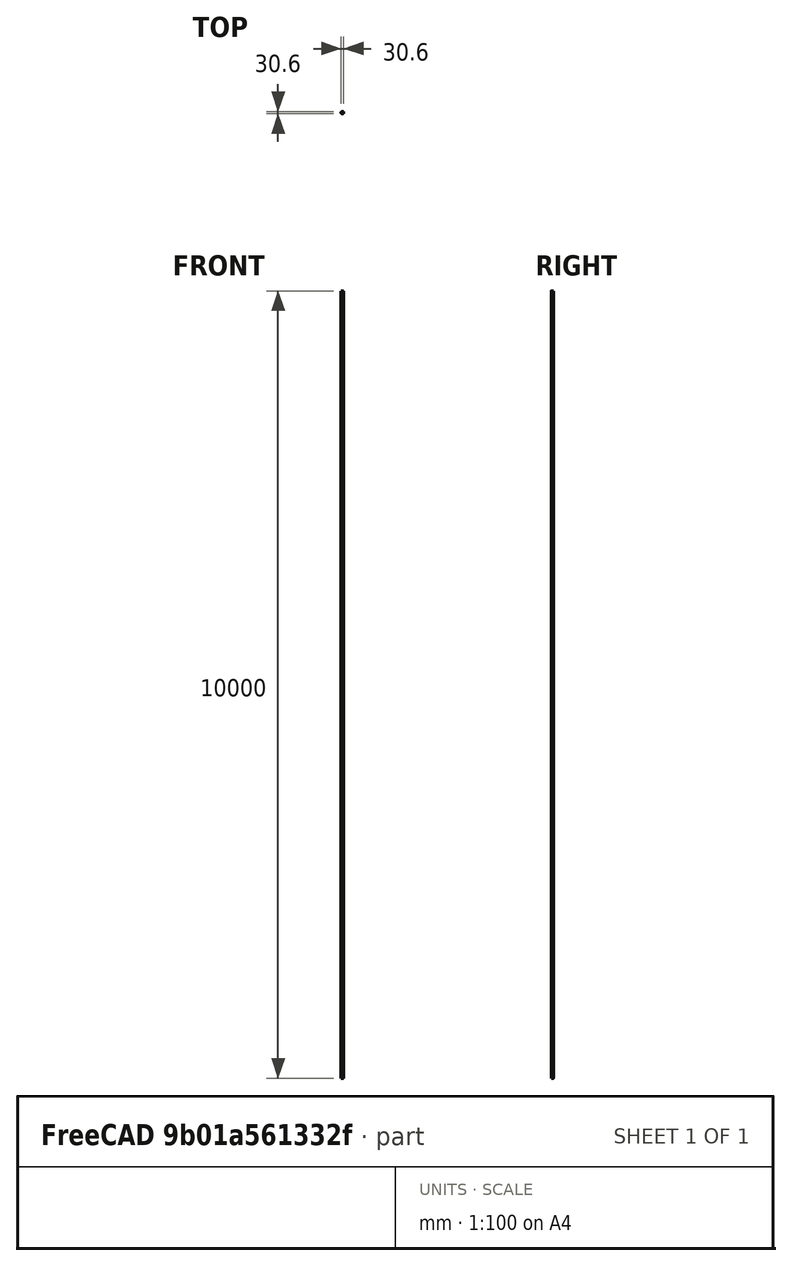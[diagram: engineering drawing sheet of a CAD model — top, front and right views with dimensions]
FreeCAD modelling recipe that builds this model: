
FCSTD DOCUMENT  (FreeCAD 0.16R)
Label: 59.4
License: All rights reserved
LicenseURL: http://en.wikipedia.org/wiki/All_rights_reserved
objects: Part::Cylinder×2, Part::Cut×1, Sketcher::SketchObject×1, PartDesign::Pocket×1, Mesh::Feature×1
note: 6 computed .brp shape members not serialized (recipe doc carries the construction recipe); baked Part::Feature solids carry a one-line shape summary decoded from their .brp

FEATURE [Part::Cylinder] Cylinder
  Angle = 360
  Height = 50
  Radius = 15.3
FEATURE [Part::Cylinder] Cylinder001
  Angle = 360
  Height = 100
  Placement = pos=(-16,0,-2) rot=(0,1,0;1.03673rad)
  Radius = 19
FEATURE [Part::Cut] Cut
  Base = -> Cylinder
  Tool = -> Cylinder001
FEATURE [Sketcher::SketchObject] Sketch
  Placement = pos=(0,0,50) rot=(0,0,1;0rad)
  Support = -> Cut [Face3]
  sketch-geometry (1):
    g0: Circle CenterX=0 CenterY=0 CenterZ=0 NormalX=0 NormalY=0 NormalZ=1 Radius=14.6
  constraints (2):
    c: Coincident(g0,g-1)
    c: Radius(g0) = 14.6
FEATURE [PartDesign::Pocket] Pocket
  Length = 5
  Sketch = -> Sketch
  Type = 1
FEATURE [Mesh::Feature] Mesh  label="Pocket (Meshed)"
